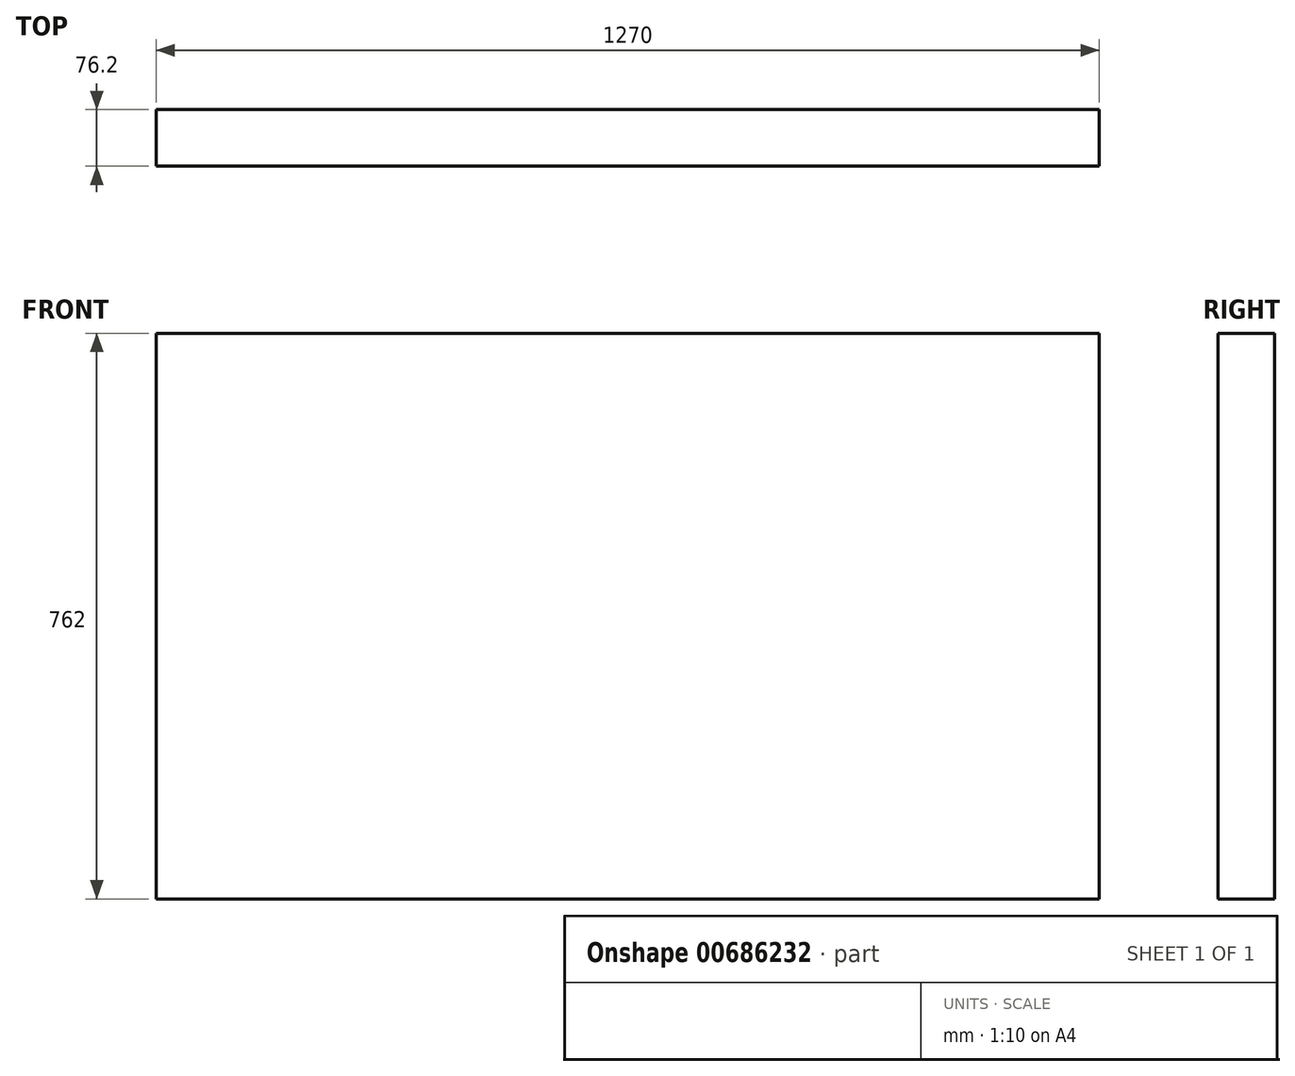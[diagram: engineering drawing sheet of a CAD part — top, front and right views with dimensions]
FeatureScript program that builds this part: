
annotation { "Feature Type Name" : "Feature", "Feature Type Description" : "" }
export const myFeature = defineFeature(function(context is Context, id is Id, definition is map)
    precondition{}
    {
        {
            var Q0;
            Q0=qCreatedBy(makeId("Front.planeOp"),FACE);
            var sketch = newSketch(context, id + "F0", { "sketchPlane" : qUnion([Q0])});
            skLineSegment(sketch, "E0.bottom", {"start": v(-635, 381) * mm, "end": v(635, 381) * mm});
            skLineSegment(sketch, "E0.top", {"start": v(-635, -381) * mm, "end": v(635, -381) * mm});
            skLineSegment(sketch, "E0.left", {"start": v(-635, 381) * mm, "end": v(-635, -381) * mm});
            skLineSegment(sketch, "E0.right", {"start": v(635, 381) * mm, "end": v(635, -381) * mm});
            skLineSegment(sketch, "E1", {"start": v(-635, -381) * mm, "end": v(635, 381) * mm, "construction": true});
            skSolve(sketch);
        }
        {
            var Q0;
            Q0=makeQuery(id+"F0.imprint","IMPRINT",FACE,{"disambiguationData":[TD([[makeQuery(id+"F0.imprint","IMPRINT",EDGE,{"derivedFrom":sQuery(id+"F0.wireOp",EDGE,"E0.bottom")}),-1.0]])]});
            extrude(context, id + "F1", {"entities" : qUnion([Q0]), "depth" : 76.2 * mm, "offsetDistance" : 25.4 * mm});
        }
    });
